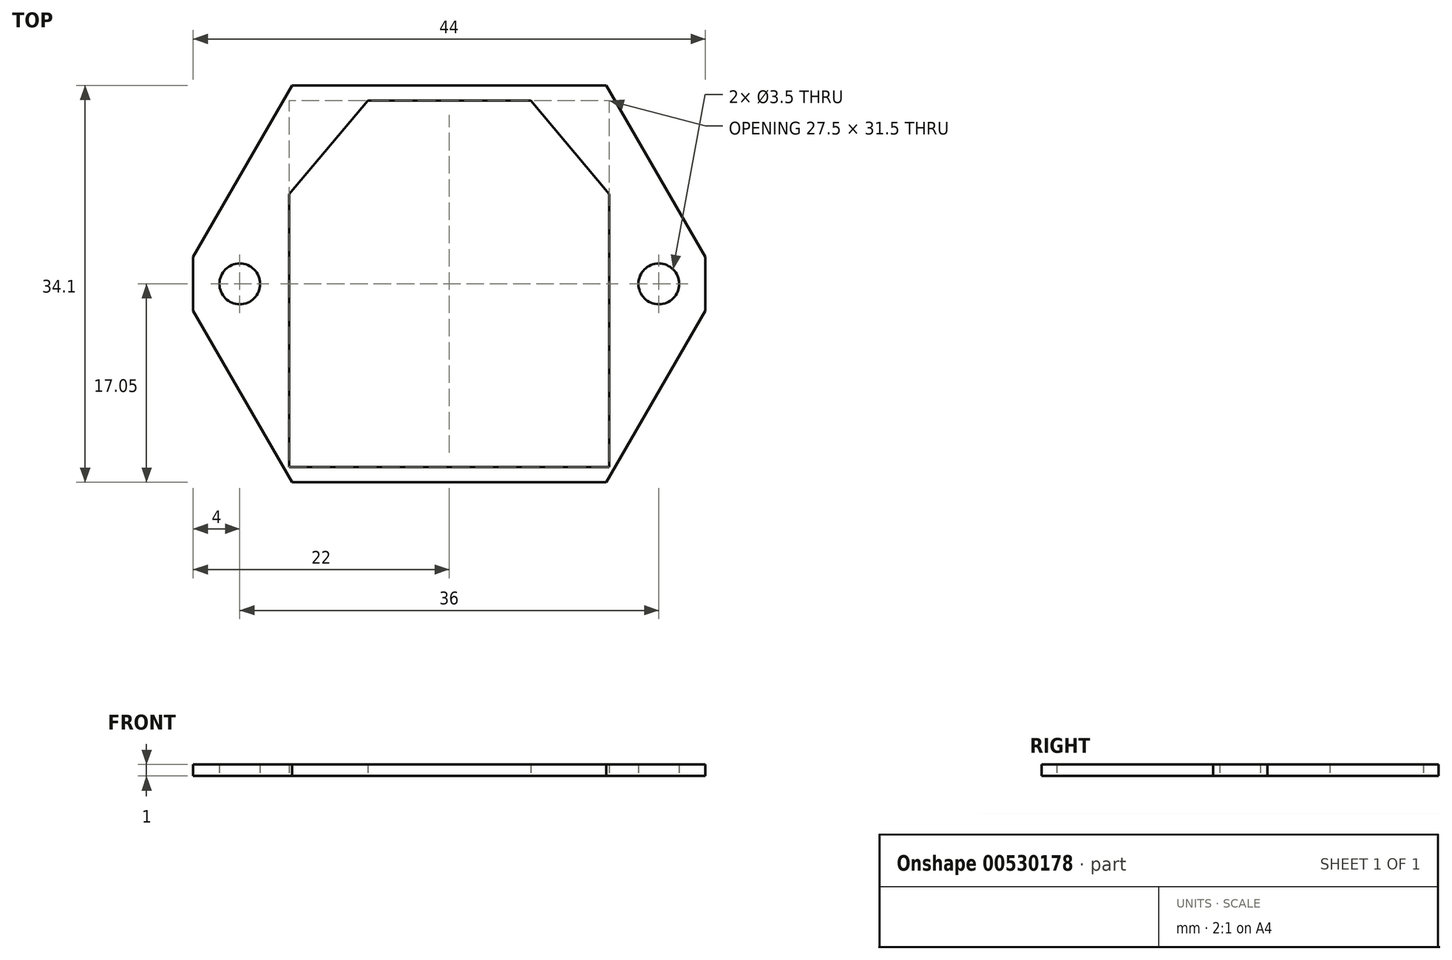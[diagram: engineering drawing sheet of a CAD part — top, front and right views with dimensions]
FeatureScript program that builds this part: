
annotation { "Feature Type Name" : "Feature", "Feature Type Description" : "" }
export const myFeature = defineFeature(function(context is Context, id is Id, definition is map)
    precondition{}
    {
        {
            var Q0;
            Q0=qCreatedBy(makeId("Top.planeOp"),FACE);
            var sketch = newSketch(context, id + "F0", { "sketchPlane" : qUnion([Q0])});
            skLineSegment(sketch, "E0.bottom", {"start": v(-13.5, 17.05) * mm, "end": v(13.5, 17.05) * mm});
            skLineSegment(sketch, "E0.top", {"start": v(-13.5, -17.05) * mm, "end": v(13.5, -17.05) * mm});
            skLineSegment(sketch, "E0.left", {"start": v(-22, 2.33) * mm, "end": v(-22, -2.33) * mm});
            skLineSegment(sketch, "E0.right", {"start": v(22, 2.33) * mm, "end": v(22, -2.33) * mm});
            skPoint(sketch, "E0.middle", {"position": v(0, 0) * mm});
            skLineSegment(sketch, "E1.bottom", {"start": v(-7, 15.75) * mm, "end": v(7, 15.75) * mm});
            skLineSegment(sketch, "E1.top", {"start": v(-13.75, -15.75) * mm, "end": v(13.75, -15.75) * mm});
            skLineSegment(sketch, "E1.left", {"start": v(-13.75, 7.7) * mm, "end": v(-13.75, -15.75) * mm});
            skLineSegment(sketch, "E1.right", {"start": v(13.75, 7.7) * mm, "end": v(13.75, -15.75) * mm});
            skCircle(sketch, "E2", {"center": v(18, 0) * mm, "radius": 1.75 * mm});
            skCircle(sketch, "E3", {"center": v(-18, 0) * mm, "radius": 1.75 * mm});
            skLineSegment(sketch, "E4", {"start": v(-13.75, 7.7) * mm, "end": v(-7, 15.75) * mm});
            skLineSegment(sketch, "E5", {"start": v(7, 15.75) * mm, "end": v(13.75, 7.7) * mm});
            skLineSegment(sketch, "E6", {"start": v(-13.5, 17.05) * mm, "end": v(-22, 2.33) * mm});
            skLineSegment(sketch, "E7", {"start": v(13.5, 17.05) * mm, "end": v(22, 2.33) * mm});
            skLineSegment(sketch, "E8", {"start": v(22, -2.33) * mm, "end": v(13.5, -17.05) * mm});
            skLineSegment(sketch, "E9", {"start": v(-22, -2.33) * mm, "end": v(-13.5, -17.05) * mm});
            skPoint(sketch, "E10.orphan", {"position": v(-22, 17.05) * mm});
            skPoint(sketch, "E11.orphan", {"position": v(-13.75, 15.75) * mm});
            skPoint(sketch, "E12.orphan", {"position": v(22, 17.05) * mm});
            skPoint(sketch, "E13.orphan", {"position": v(13.75, 15.75) * mm});
            skPoint(sketch, "E14.orphan", {"position": v(22, -17.05) * mm});
            skPoint(sketch, "E15.orphan", {"position": v(-22, -17.05) * mm});
            skSolve(sketch);
        }
        {
            var Q0;
            Q0 = qSketchRegion(id + "F0", true);
            extrude(context, id + "F1", {"entities" : qUnion([Q0]), "depth" : 1 * mm, "offsetDistance" : 25 * mm});
        }
    });
